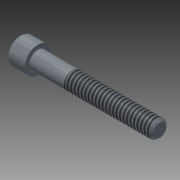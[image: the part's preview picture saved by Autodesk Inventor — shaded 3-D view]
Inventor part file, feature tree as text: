
AUTODESK INVENTOR PART (.ipt)
format: ipt  version: 2014 (Build 180170000, 170)  size: 164,352 bytes
history: native  units: mm (DEFAULTED — no unit token found)
features: sketch x2, extrude x1, plane x1, fillet x1
ambient origin geometry x7: Origin, YZ Plane, XY Plane, X Axis, Y Axis, Z Axis, Center Point
bodies: Solid1 (feature_tree), Body (feature_tree)
feature tree (5):
  extrude  "Slot"  Depth=3.1751mm
  plane  "Work Plane1"
  fillet  "Fillet2"  Radius=6.35mm
  sketch  "Sketch1"  dims[d1=31.75mm d2=3.1751mm d3=6.35mm]
  sketch  "Sketch2"  dims[d4=3.048mm d5=60.0deg d6=6.35mm d7=6.35mm d8=5.513926mm d9=9.525mm d10=90.0deg d11=10.0mm d12=0.0mm d13=31.75mm d14=0.0mm d15=0.75565mm d16=0.75565mm d17=0.635mm d19=0.0mm d26=44.45mm d27=45.0deg d28=0.0mm d29=0.0mm d30=0.1778mm]
